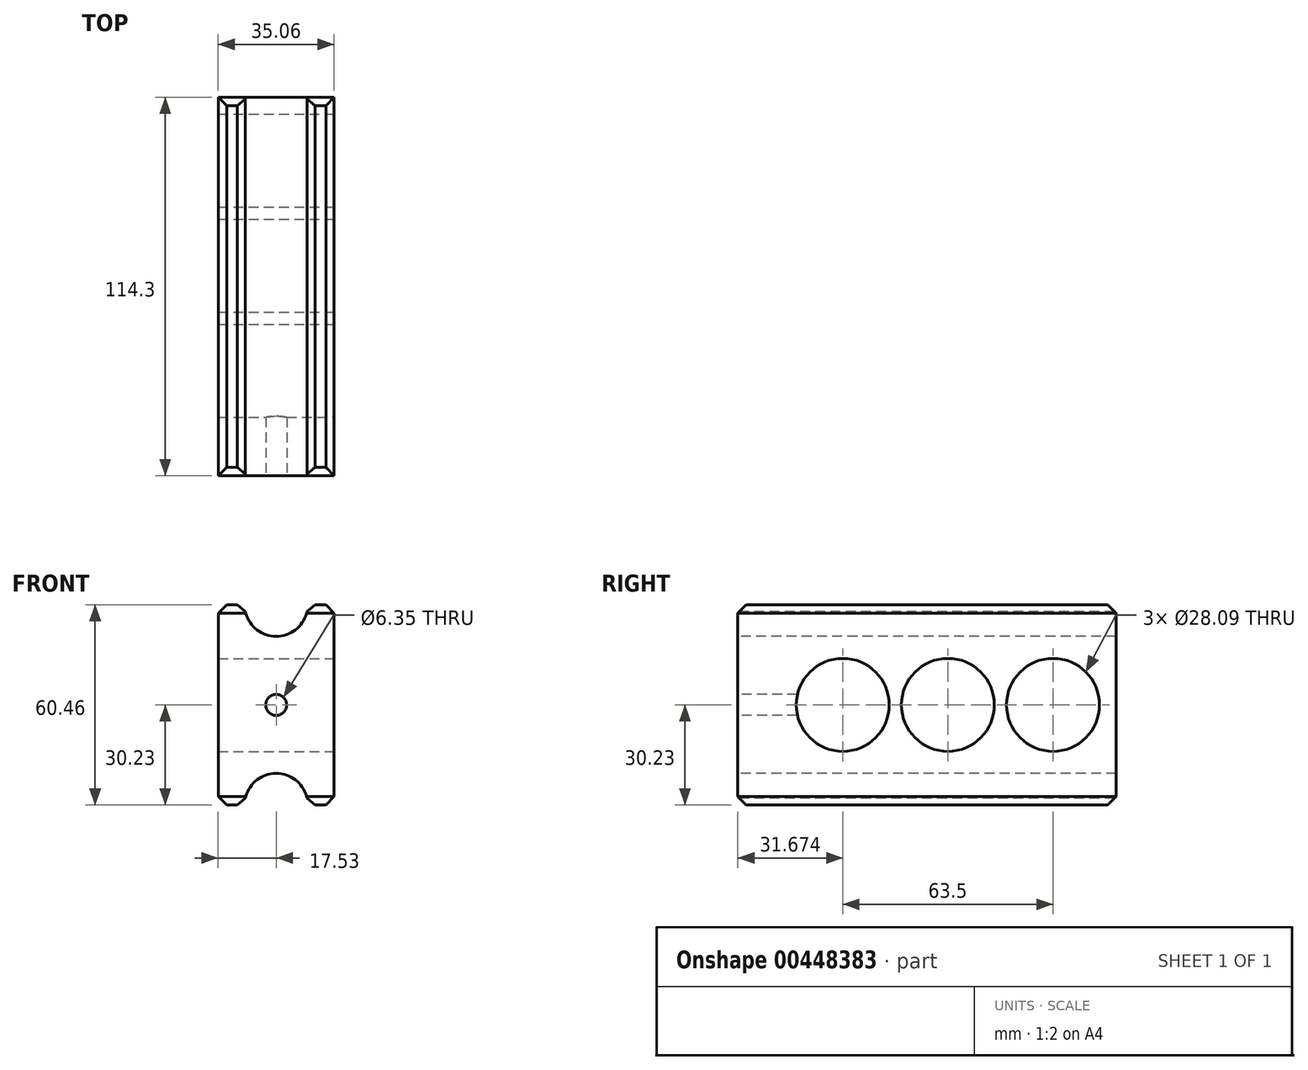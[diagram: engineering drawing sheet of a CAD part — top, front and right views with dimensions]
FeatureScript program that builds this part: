
annotation { "Feature Type Name" : "Feature", "Feature Type Description" : "" }
export const myFeature = defineFeature(function(context is Context, id is Id, definition is map)
    precondition{}
    {
        {
            var Q0;
            Q0=qCreatedBy(makeId("Front.planeOp"),FACE);
            var sketch = newSketch(context, id + "F0", { "sketchPlane" : qUnion([Q0])});
            skLineSegment(sketch, "E0.bottom", {"start": v(-17.53, -30.23) * mm, "end": v(17.53, -30.23) * mm});
            skLineSegment(sketch, "E0.top", {"start": v(-17.53, 30.23) * mm, "end": v(17.53, 30.23) * mm});
            skLineSegment(sketch, "E0.left", {"start": v(-17.53, -30.23) * mm, "end": v(-17.53, 30.23) * mm});
            skLineSegment(sketch, "E0.right", {"start": v(17.53, -30.23) * mm, "end": v(17.53, 30.23) * mm});
            skPoint(sketch, "E0.middle", {"position": v(0, 0) * mm});
            skSolve(sketch);
        }
        {
            var Q0;
            Q0 = qSketchRegion(id + "F0", true);
            extrude(context, id + "F1", {"entities" : qUnion([Q0]), "depth" : 114.3 * mm});
        }
        {
            var Q0;
            Q0=makeQuery(id+"F1.opExtrude","SWEPT_FACE",FACE,{"disambiguationData":[OSD([sQuery(id+"F0.wireOp",EDGE,"E0.right")])]});
            var sketch = newSketch(context, id + "F2", { "sketchPlane" : qUnion([Q0])});
            skCircle(sketch, "E1", {"center": v(-19.13, 0) * mm, "radius": 14.05 * mm});
            skCircle(sketch, "E2", {"center": v(-50.88, 0) * mm, "radius": 14.05 * mm});
            skCircle(sketch, "E3", {"center": v(-82.63, 0) * mm, "radius": 14.05 * mm});
            skSolve(sketch);
        }
        {
            var Q0;
            Q0 = qSketchRegion(id + "F2", true);
            extrude(context, id + "F3", {"entities" : qUnion([Q0]), "operationType" : NewBodyOperationType.REMOVE, "endBound" : BoundingType.THROUGH_ALL, "oppositeDirection" : true, "depth" : 25.4 * mm});
        }
        {
            var Q0;
            Q0=makeQuery(id+"F1.opExtrude","CAP_FACE",FACE,{"disambiguationData":[OSD([sQuery(id+"F0.wireOp",EDGE,"E0.bottom"),sQuery(id+"F0.wireOp",EDGE,"E0.top"),sQuery(id+"F0.wireOp",EDGE,"E0.left"),sQuery(id+"F0.wireOp",EDGE,"E0.right")])],"isStart":false});
            var sketch = newSketch(context, id + "F4", { "sketchPlane" : qUnion([Q0])});
            skCircle(sketch, "E4", {"center": v(0, 0) * mm, "radius": 3.18 * mm});
            skSolve(sketch);
        }
        {
            var Q0;
            Q0 = qSketchRegion(id + "F4", true);
            extrude(context, id + "F5", {"entities" : qUnion([Q0]), "operationType" : NewBodyOperationType.REMOVE, "oppositeDirection" : true, "depth" : 25.4 * mm});
        }
        {
            var Q0;
            Q0=makeQuery(id+"F1.opExtrude","CAP_FACE",FACE,{"disambiguationData":[OSD([sQuery(id+"F0.wireOp",EDGE,"E0.bottom"),sQuery(id+"F0.wireOp",EDGE,"E0.top"),sQuery(id+"F0.wireOp",EDGE,"E0.left"),sQuery(id+"F0.wireOp",EDGE,"E0.right")])],"isStart":false});
            var sketch = newSketch(context, id + "F6", { "sketchPlane" : qUnion([Q0])});
            skCircle(sketch, "E5", {"center": v(0, 30.23) * mm, "radius": 9.53 * mm});
            skCircle(sketch, "E6", {"center": v(0, -30.23) * mm, "radius": 9.53 * mm});
            skSolve(sketch);
        }
        {
            var Q0;
            Q0 = qSketchRegion(id + "F6", true);
            extrude(context, id + "F7", {"entities" : qUnion([Q0]), "operationType" : NewBodyOperationType.REMOVE, "endBound" : BoundingType.THROUGH_ALL, "oppositeDirection" : true, "depth" : 25.4 * mm});
        }
        {
            var Q0;
            {var subQ1=sQuery(id+"F0.wireOp",EDGE,"E0.left");var subQ2=sQuery(id+"F0.wireOp",EDGE,"E0.top");Q0=makeQuery(id+"F7.boolean.opBoolean","SPLIT",FACE,{"disambiguationData":[TD([makeQuery(id+"F1.opExtrude","SWEPT_FACE",FACE,{"disambiguationData":[OSD([subQ1])]})])],"derivedFrom":makeQuery(id+"F1.opExtrude","SWEPT_FACE",FACE,{"disambiguationData":[OSD([subQ2])]})});}
            var Q1;
            {var subQ0=sQuery(id+"F0.wireOp",EDGE,"E0.right");var subQ2=sQuery(id+"F0.wireOp",EDGE,"E0.top");Q1=makeQuery(id+"F7.boolean.opBoolean","SPLIT",FACE,{"disambiguationData":[TD([makeQuery(id+"F1.opExtrude","SWEPT_FACE",FACE,{"disambiguationData":[OSD([subQ0])]})])],"derivedFrom":makeQuery(id+"F1.opExtrude","SWEPT_FACE",FACE,{"disambiguationData":[OSD([subQ2])]})});}
            var Q2;
            {var subQ1=sQuery(id+"F0.wireOp",EDGE,"E0.left");var subQ3=sQuery(id+"F0.wireOp",EDGE,"E0.bottom");Q2=makeQuery(id+"F7.boolean.opBoolean","SPLIT",FACE,{"disambiguationData":[TD([makeQuery(id+"F1.opExtrude","SWEPT_FACE",FACE,{"disambiguationData":[OSD([subQ1])]})])],"derivedFrom":makeQuery(id+"F1.opExtrude","SWEPT_FACE",FACE,{"disambiguationData":[OSD([subQ3])]})});}
            var Q3;
            {var subQ0=sQuery(id+"F0.wireOp",EDGE,"E0.right");var subQ3=sQuery(id+"F0.wireOp",EDGE,"E0.bottom");Q3=makeQuery(id+"F7.boolean.opBoolean","SPLIT",FACE,{"disambiguationData":[TD([makeQuery(id+"F1.opExtrude","SWEPT_FACE",FACE,{"disambiguationData":[OSD([subQ0])]})])],"derivedFrom":makeQuery(id+"F1.opExtrude","SWEPT_FACE",FACE,{"disambiguationData":[OSD([subQ3])]})});}
            chamfer(context, id + "F8", {"entities" : qUnion([Q0, Q1, Q2, Q3]), "width" : 2.54 * mm, "tangentPropagation" : true});
        }
    });
